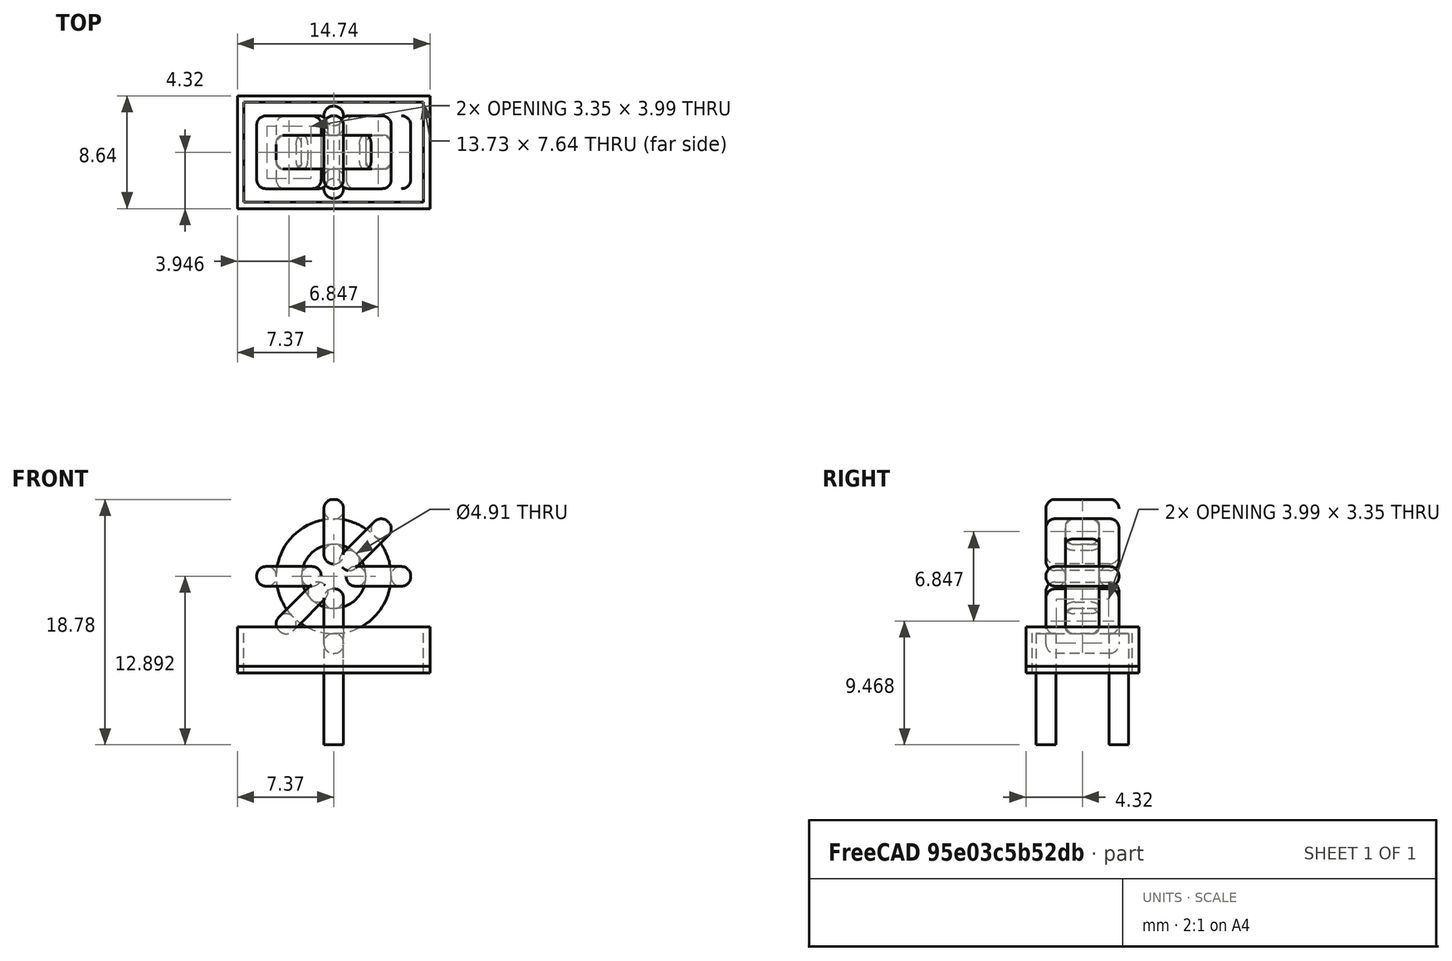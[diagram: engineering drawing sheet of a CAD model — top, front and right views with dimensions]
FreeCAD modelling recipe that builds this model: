
FCSTD DOCUMENT  (FreeCAD 0.16R6703 (Git))
Label: L_Toroid_Vertical_L14.7mm_W8.6mm_P5.58mm_Pulse_KM-1
License: All rights reserved
LicenseURL: http://en.wikipedia.org/wiki/All_rights_reserved
objects: Sketcher::SketchObject×8, PartDesign::Pad×8, PartDesign::Fillet×5, Spreadsheet::Sheet×1
note: 29 computed .brp shape members not serialized (recipe doc carries the construction recipe); baked Part::Feature solids carry a one-line shape summary decoded from their .brp

FEATURE [Spreadsheet::Sheet] Spreadsheet  label="dimensions"
  cells = A1=Wx; B1(Wx)=11.784; C1(WW)=4.91; D1(iWx)=14.73; A2=Wy; B2(Wy)=5.58; D2(iWy)=8.640000000000001; A3=RM; B3(RMx)=5.58; C3(RMy)=0; A4=d_wire; B4(d_wire)=1.5; A5=H; B5(H)=14.73; A6=offsetx; B6(offsetx)=7.365
FEATURE [Sketcher::SketchObject] Sketch
  Placement = pos=(0,-2.79,0) rot=(1,0,0;1.5708rad)
  expr: Placement.Base.y = -Spreadsheet.RMx / 2
  expr: Constraints[0] = Spreadsheet.Wx / 2 - Spreadsheet.d_wire
  expr: Constraints[4] = Spreadsheet.WW / 2
  expr: Constraints[2] = Spreadsheet.Wx / 2 + Spreadsheet.d_wire + 0.5
  sketch-geometry (2):
    g0: Circle CenterX=0 CenterY=7.892 CenterZ=0 NormalX=0 NormalY=0 NormalZ=1 Radius=4.392
    g1: Circle CenterX=0 CenterY=7.892 CenterZ=0 NormalX=0 NormalY=0 NormalZ=1 Radius=2.455
  constraints (5):
    c: Radius(g0) = 4.392
    c: DistanceX(g-1,g0) = 0
    c: DistanceY(g-1,g0) = 7.892
    c: Coincident(g1,g0)
    c: Radius(g1) = 2.455
FEATURE [PartDesign::Pad] Pad
  Length = 2.58
  Length2 = 100
  Midplane = true
  Placement = pos=(0,-2.79,0) rot=(1,0,0;1.5708rad)
  Sketch = -> Sketch
  Type = 0
  expr: Length = Spreadsheet.Wy - 2 * Spreadsheet.d_wire
FEATURE [Sketcher::SketchObject] Sketch001
  Placement = pos=(0,0,2) rot=(0,0,1;0rad)
  expr: Placement.Base.z = 0.5 + Spreadsheet.d_wire
  expr: Constraints[4] = Spreadsheet.RMy
  expr: Constraints[2] = -Spreadsheet.RMx
  expr: Constraints[1] = Spreadsheet.d_wire / 2
  sketch-geometry (2):
    g0: Circle CenterX=0 CenterY=0 CenterZ=0 NormalX=0 NormalY=0 NormalZ=1 Radius=0.75
    g1: Circle CenterX=0 CenterY=-5.58 CenterZ=0 NormalX=0 NormalY=0 NormalZ=1 Radius=0.75
  constraints (5):
    c: Equal(g0,g1)
    c: Radius(g0) = 0.75
    c: DistanceY(g-1,g1) = -5.58
    c: Coincident(g0,g-1)
    c: DistanceX(g-1,g1) = 0
FEATURE [PartDesign::Pad] Pad001
  Length = 1.5
  Length2 = 7
  Placement = pos=(0,0,2) rot=(0,0,1;0rad)
  Reversed = true
  Sketch = -> Sketch001
  Type = 4
  expr: Length2 = 5.5 + Spreadsheet.d_wire
  expr: Length = Spreadsheet.d_wire
FEATURE [PartDesign::Fillet] Fillet
  Base = -> Pad [Edge6,Edge3,Edge2]
  Placement = pos=(0,-2.79,0) rot=(1,0,0;1.5708rad)
  Radius = 0.5
FEATURE [Sketcher::SketchObject] Sketch003
  Placement = pos=(0,0,7.892) rot=(1,0,0;3.14159rad)
  expr: Constraints[18] = Spreadsheet.d_wire
  expr: Constraints[16] = Spreadsheet.d_wire
  expr: Constraints[19] = Spreadsheet.d_wire
  expr: Constraints[17] = Spreadsheet.d_wire
  expr: Placement.Base.y = -1 * (Spreadsheet.RMx - Spreadsheet.Wy) / 2
  expr: Constraints[21] = (Spreadsheet.Wx - Spreadsheet.WW) / 2 - Spreadsheet.d_wire
  expr: Constraints[22] = Spreadsheet.Wx / 2 - Spreadsheet.d_wire
  expr: Constraints[43] = Spreadsheet.d_wire
  expr: Constraints[48] = Spreadsheet.Wx - Spreadsheet.d_wire * 2
  expr: Constraints[49] = Spreadsheet.Wy
  expr: Placement.Base.z = Spreadsheet.Wx / 2 + Spreadsheet.d_wire + 0.5
  sketch-geometry (16):
    g0: LineSegment StartX=-0.955 StartY=0 StartZ=0 EndX=-5.892 EndY=0 EndZ=0
    g1: LineSegment StartX=-5.892 StartY=0 StartZ=0 EndX=-5.892 EndY=5.58 EndZ=0
    g2: LineSegment StartX=-5.892 StartY=5.58 StartZ=0 EndX=-0.955 EndY=5.58 EndZ=0
    g3: LineSegment StartX=-0.955 StartY=5.58 StartZ=0 EndX=-0.955 EndY=0 EndZ=0
    g4: LineSegment StartX=-4.392 StartY=4.08 StartZ=0 EndX=-2.455 EndY=4.08 EndZ=0
    g5: LineSegment StartX=-2.455 StartY=4.08 StartZ=0 EndX=-2.455 EndY=1.5 EndZ=0
    g6: LineSegment StartX=-2.455 StartY=1.5 StartZ=0 EndX=-4.392 EndY=1.5 EndZ=0
    g7: LineSegment StartX=-4.392 StartY=1.5 StartZ=0 EndX=-4.392 EndY=4.08 EndZ=0
    g8: LineSegment StartX=0.955 StartY=5.58 StartZ=0 EndX=5.892 EndY=5.58 EndZ=0
    g9: LineSegment StartX=5.892 StartY=5.58 StartZ=0 EndX=5.892 EndY=0 EndZ=0
    g10: LineSegment StartX=5.892 StartY=0 StartZ=0 EndX=0.955 EndY=0 EndZ=0
    g11: LineSegment StartX=0.955 StartY=0 StartZ=0 EndX=0.955 EndY=5.58 EndZ=0
    g12: LineSegment StartX=2.455 StartY=4.08 StartZ=0 EndX=4.392 EndY=4.08 EndZ=0
    g13: LineSegment StartX=4.392 StartY=4.08 StartZ=0 EndX=4.392 EndY=1.5 EndZ=0
    g14: LineSegment StartX=4.392 StartY=1.5 StartZ=0 EndX=2.455 EndY=1.5 EndZ=0
    g15: LineSegment StartX=2.455 StartY=1.5 StartZ=0 EndX=2.455 EndY=4.08 EndZ=0
  constraints (50):
    c: Horizontal(g0)
    c: Coincident(g1,g0)
    c: Vertical(g1)
    c: Coincident(g2,g1)
    c: Horizontal(g2)
    c: Coincident(g3,g2)
    c: Coincident(g3,g0)
    c: Vertical(g3)
    c: Coincident(g4,g5)
    c: Coincident(g5,g6)
    c: Coincident(g6,g7)
    c: Coincident(g7,g4)
    c: Horizontal(g4)
    c: Horizontal(g6)
    c: Vertical(g5)
    c: Vertical(g7)
    c: DistanceX(g1,g4) = 1.5
    c: DistanceY(g4,g1) = 1.5
    c: DistanceX(g5,g0) = 1.5
    c: DistanceY(g0,g5) = 1.5
    c: DistanceY(g-1,g0) = 0
    c: DistanceX(g6,g6) = 1.937
    c: DistanceX(g6,g-1) = 4.392
    c: Coincident(g8,g9)
    c: Coincident(g9,g10)
    c: Coincident(g10,g11)
    c: Coincident(g11,g8)
    c: Horizontal(g8)
    c: Horizontal(g10)
    c: Vertical(g9)
    c: Vertical(g11)
    c: Coincident(g12,g13)
    c: Coincident(g13,g14)
    c: Coincident(g14,g15)
    c: Coincident(g15,g12)
    c: Horizontal(g12)
    c: Horizontal(g14)
    c: Vertical(g13)
    c: Vertical(g15)
    c: DistanceY(g8,g2) = 0
    c: DistanceY(g10,g0) = 0
    c: DistanceY(g14,g5) = 0
    c: DistanceY(g12,g4) = 0
    c: DistanceX(g8,g12) = 1.5
    c: Equal(g8,g2)
    c: Equal(g12,g4)
    c: Equal(g9,g1)
    c: Equal(g13,g7)
    c: DistanceX(g4,g12) = 8.784
    c: DistanceY(g0,g1) = 5.58
FEATURE [PartDesign::Pad] Pad002
  Length = 1.5
  Length2 = 100
  Midplane = true
  Placement = pos=(0,0,7.892) rot=(1,0,0;3.14159rad)
  Sketch = -> Sketch003
  Type = 0
  expr: Length = Spreadsheet.d_wire
FEATURE [PartDesign::Fillet] Fillet001
  Base = -> Pad002 [Edge38,Edge41,Edge42,Edge43,Edge29,Edge32,Edge33,Edge34,Edge25,Edge35,Edge36,Edge13,Edge14,Edge15,Edge16,Edge17,Edge18,Edge19,Edge1,Edge2,Edge3,Edge4,Edge5,Edge6,Edge7,Edge37,Edge39,Edge40,Edge20,Edge23,Edge24,Edge21,Edge22,Edge8,Edge9,Edge10,Edge11,Edge12,Edge26,Edge27,+8 more]
  Placement = pos=(0,0,7.892) rot=(1,0,0;3.14159rad)
  Radius = 0.705
  expr: Radius = Spreadsheet.d_wire * 0.47
FEATURE [Sketcher::SketchObject] Sketch004
  Placement = pos=(0,0,7.892) rot=(0.92388,0,0.382683;3.14159rad)
  expr: Constraints[18] = Spreadsheet.d_wire
  expr: Constraints[16] = Spreadsheet.d_wire
  expr: Constraints[19] = Spreadsheet.d_wire
  expr: Constraints[17] = Spreadsheet.d_wire
  expr: Placement.Base.y = -1 * (Spreadsheet.RMx - Spreadsheet.Wy) / 2
  expr: Constraints[21] = (Spreadsheet.Wx - Spreadsheet.WW) / 2 - Spreadsheet.d_wire
  expr: Constraints[22] = Spreadsheet.Wx / 2 - Spreadsheet.d_wire
  expr: Constraints[43] = Spreadsheet.d_wire
  expr: Constraints[48] = Spreadsheet.Wx - 2 * Spreadsheet.d_wire
  expr: Constraints[49] = Spreadsheet.Wy
  expr: Placement.Base.z = Spreadsheet.Wx / 2 + Spreadsheet.d_wire + 0.5
  sketch-geometry (16):
    g0: LineSegment StartX=-0.955 StartY=0 StartZ=0 EndX=-5.892 EndY=0 EndZ=0
    g1: LineSegment StartX=-5.892 StartY=0 StartZ=0 EndX=-5.892 EndY=5.58 EndZ=0
    g2: LineSegment StartX=-5.892 StartY=5.58 StartZ=0 EndX=-0.955 EndY=5.58 EndZ=0
    g3: LineSegment StartX=-0.955 StartY=5.58 StartZ=0 EndX=-0.955 EndY=0 EndZ=0
    g4: LineSegment StartX=-4.392 StartY=4.08 StartZ=0 EndX=-2.455 EndY=4.08 EndZ=0
    g5: LineSegment StartX=-2.455 StartY=4.08 StartZ=0 EndX=-2.455 EndY=1.5 EndZ=0
    g6: LineSegment StartX=-2.455 StartY=1.5 StartZ=0 EndX=-4.392 EndY=1.5 EndZ=0
    g7: LineSegment StartX=-4.392 StartY=1.5 StartZ=0 EndX=-4.392 EndY=4.08 EndZ=0
    g8: LineSegment StartX=0.955 StartY=5.58 StartZ=0 EndX=5.892 EndY=5.58 EndZ=0
    g9: LineSegment StartX=5.892 StartY=5.58 StartZ=0 EndX=5.892 EndY=0 EndZ=0
    g10: LineSegment StartX=5.892 StartY=0 StartZ=0 EndX=0.955 EndY=0 EndZ=0
    g11: LineSegment StartX=0.955 StartY=0 StartZ=0 EndX=0.955 EndY=5.58 EndZ=0
    g12: LineSegment StartX=2.455 StartY=4.08 StartZ=0 EndX=4.392 EndY=4.08 EndZ=0
    g13: LineSegment StartX=4.392 StartY=4.08 StartZ=0 EndX=4.392 EndY=1.5 EndZ=0
    g14: LineSegment StartX=4.392 StartY=1.5 StartZ=0 EndX=2.455 EndY=1.5 EndZ=0
    g15: LineSegment StartX=2.455 StartY=1.5 StartZ=0 EndX=2.455 EndY=4.08 EndZ=0
  constraints (50):
    c: Horizontal(g0)
    c: Coincident(g1,g0)
    c: Vertical(g1)
    c: Coincident(g2,g1)
    c: Horizontal(g2)
    c: Coincident(g3,g2)
    c: Coincident(g3,g0)
    c: Vertical(g3)
    c: Coincident(g4,g5)
    c: Coincident(g5,g6)
    c: Coincident(g6,g7)
    c: Coincident(g7,g4)
    c: Horizontal(g4)
    c: Horizontal(g6)
    c: Vertical(g5)
    c: Vertical(g7)
    c: DistanceX(g1,g4) = 1.5
    c: DistanceY(g4,g1) = 1.5
    c: DistanceX(g5,g0) = 1.5
    c: DistanceY(g0,g5) = 1.5
    c: DistanceY(g-1,g0) = 0
    c: DistanceX(g6,g6) = 1.937
    c: DistanceX(g6,g-1) = 4.392
    c: Coincident(g8,g9)
    c: Coincident(g9,g10)
    c: Coincident(g10,g11)
    c: Coincident(g11,g8)
    c: Horizontal(g8)
    c: Horizontal(g10)
    c: Vertical(g9)
    c: Vertical(g11)
    c: Coincident(g12,g13)
    c: Coincident(g13,g14)
    c: Coincident(g14,g15)
    c: Coincident(g15,g12)
    c: Horizontal(g12)
    c: Horizontal(g14)
    c: Vertical(g13)
    c: Vertical(g15)
    c: DistanceY(g8,g2) = 0
    c: DistanceY(g10,g0) = 0
    c: DistanceY(g14,g5) = 0
    c: DistanceY(g12,g4) = 0
    c: DistanceX(g8,g12) = 1.5
    c: Equal(g8,g2)
    c: Equal(g12,g4)
    c: Equal(g9,g1)
    c: Equal(g13,g7)
    c: DistanceX(g4,g12) = 8.784
    c: DistanceY(g0,g1) = 5.58
FEATURE [PartDesign::Pad] Pad003
  Length = 1.5
  Length2 = 100
  Midplane = true
  Placement = pos=(0,0,7.892) rot=(0.92388,0,0.382683;3.14159rad)
  Sketch = -> Sketch004
  Type = 0
  expr: Length = Spreadsheet.d_wire
FEATURE [PartDesign::Fillet] Fillet002
  Base = -> Pad003 [Edge38,Edge41,Edge42,Edge43,Edge29,Edge32,Edge33,Edge34,Edge25,Edge35,Edge36,Edge13,Edge14,Edge15,Edge16,Edge17,Edge18,Edge19,Edge1,Edge2,Edge3,Edge4,Edge5,Edge6,Edge7,Edge37,Edge39,Edge40,Edge20,Edge23,Edge24,Edge21,Edge22,Edge8,Edge9,Edge10,Edge11,Edge12,Edge26,Edge27,+8 more]
  Placement = pos=(0,0,7.892) rot=(0.92388,0,0.382683;3.14159rad)
  Radius = 0.705
  expr: Radius = Spreadsheet.d_wire * 0.47
FEATURE [Sketcher::SketchObject] Sketch005
  Placement = pos=(0,0,7.892) rot=(0.92388,0,-0.382683;3.14159rad)
  expr: Constraints[18] = Spreadsheet.d_wire
  expr: Constraints[16] = Spreadsheet.d_wire
  expr: Constraints[19] = Spreadsheet.d_wire
  expr: Constraints[17] = Spreadsheet.d_wire
  expr: Placement.Base.y = -1 * (Spreadsheet.RMx - Spreadsheet.Wy) / 2
  expr: Constraints[21] = (Spreadsheet.Wx - Spreadsheet.WW) / 2 - Spreadsheet.d_wire
  expr: Constraints[22] = Spreadsheet.Wx / 2 - Spreadsheet.d_wire
  expr: Constraints[43] = Spreadsheet.d_wire
  expr: Constraints[48] = Spreadsheet.Wx - 2 * Spreadsheet.d_wire
  expr: Constraints[49] = Spreadsheet.Wy
  expr: Placement.Base.z = Spreadsheet.Wx / 2 + Spreadsheet.d_wire + 0.5
  sketch-geometry (16):
    g0: LineSegment StartX=-0.955 StartY=0 StartZ=0 EndX=-5.892 EndY=0 EndZ=0
    g1: LineSegment StartX=-5.892 StartY=0 StartZ=0 EndX=-5.892 EndY=5.58 EndZ=0
    g2: LineSegment StartX=-5.892 StartY=5.58 StartZ=0 EndX=-0.955 EndY=5.58 EndZ=0
    g3: LineSegment StartX=-0.955 StartY=5.58 StartZ=0 EndX=-0.955 EndY=0 EndZ=0
    g4: LineSegment StartX=-4.392 StartY=4.08 StartZ=0 EndX=-2.455 EndY=4.08 EndZ=0
    g5: LineSegment StartX=-2.455 StartY=4.08 StartZ=0 EndX=-2.455 EndY=1.5 EndZ=0
    g6: LineSegment StartX=-2.455 StartY=1.5 StartZ=0 EndX=-4.392 EndY=1.5 EndZ=0
    g7: LineSegment StartX=-4.392 StartY=1.5 StartZ=0 EndX=-4.392 EndY=4.08 EndZ=0
    g8: LineSegment StartX=0.955 StartY=5.58 StartZ=0 EndX=5.892 EndY=5.58 EndZ=0
    g9: LineSegment StartX=5.892 StartY=5.58 StartZ=0 EndX=5.892 EndY=0 EndZ=0
    g10: LineSegment StartX=5.892 StartY=0 StartZ=0 EndX=0.955 EndY=0 EndZ=0
    g11: LineSegment StartX=0.955 StartY=0 StartZ=0 EndX=0.955 EndY=5.58 EndZ=0
    g12: LineSegment StartX=2.455 StartY=4.08 StartZ=0 EndX=4.392 EndY=4.08 EndZ=0
    g13: LineSegment StartX=4.392 StartY=4.08 StartZ=0 EndX=4.392 EndY=1.5 EndZ=0
    g14: LineSegment StartX=4.392 StartY=1.5 StartZ=0 EndX=2.455 EndY=1.5 EndZ=0
    g15: LineSegment StartX=2.455 StartY=1.5 StartZ=0 EndX=2.455 EndY=4.08 EndZ=0
  constraints (50):
    c: Horizontal(g0)
    c: Coincident(g1,g0)
    c: Vertical(g1)
    c: Coincident(g2,g1)
    c: Horizontal(g2)
    c: Coincident(g3,g2)
    c: Coincident(g3,g0)
    c: Vertical(g3)
    c: Coincident(g4,g5)
    c: Coincident(g5,g6)
    c: Coincident(g6,g7)
    c: Coincident(g7,g4)
    c: Horizontal(g4)
    c: Horizontal(g6)
    c: Vertical(g5)
    c: Vertical(g7)
    c: DistanceX(g1,g4) = 1.5
    c: DistanceY(g4,g1) = 1.5
    c: DistanceX(g5,g0) = 1.5
    c: DistanceY(g0,g5) = 1.5
    c: DistanceY(g-1,g0) = 0
    c: DistanceX(g6,g6) = 1.937
    c: DistanceX(g6,g-1) = 4.392
    c: Coincident(g8,g9)
    c: Coincident(g9,g10)
    c: Coincident(g10,g11)
    c: Coincident(g11,g8)
    c: Horizontal(g8)
    c: Horizontal(g10)
    c: Vertical(g9)
    c: Vertical(g11)
    c: Coincident(g12,g13)
    c: Coincident(g13,g14)
    c: Coincident(g14,g15)
    c: Coincident(g15,g12)
    c: Horizontal(g12)
    c: Horizontal(g14)
    c: Vertical(g13)
    c: Vertical(g15)
    c: DistanceY(g8,g2) = 0
    c: DistanceY(g10,g0) = 0
    c: DistanceY(g14,g5) = 0
    c: DistanceY(g12,g4) = 0
    c: DistanceX(g8,g12) = 1.5
    c: Equal(g8,g2)
    c: Equal(g12,g4)
    c: Equal(g9,g1)
    c: Equal(g13,g7)
    c: DistanceX(g4,g12) = 8.784
    c: DistanceY(g0,g1) = 5.58
FEATURE [PartDesign::Pad] Pad004
  Length = 1.5
  Length2 = 100
  Midplane = true
  Placement = pos=(0,0,7.892) rot=(0.92388,0,-0.382683;3.14159rad)
  Sketch = -> Sketch005
  Type = 0
  expr: Length = Spreadsheet.d_wire
FEATURE [PartDesign::Fillet] Fillet003
  Base = -> Pad004 [Edge38,Edge41,Edge42,Edge43,Edge29,Edge32,Edge33,Edge34,Edge25,Edge35,Edge36,Edge13,Edge14,Edge15,Edge16,Edge17,Edge18,Edge19,Edge1,Edge2,Edge3,Edge4,Edge5,Edge6,Edge7,Edge37,Edge39,Edge40,Edge20,Edge23,Edge24,Edge21,Edge22,Edge8,Edge9,Edge10,Edge11,Edge12,Edge26,Edge27,+8 more]
  Placement = pos=(0,0,7.892) rot=(0.92388,0,-0.382683;3.14159rad)
  Radius = 0.705
  expr: Radius = Spreadsheet.d_wire * 0.47
FEATURE [Sketcher::SketchObject] Sketch006
  Placement = pos=(0,0,7.892) rot=(0.707107,0,0.707107;3.14159rad)
  expr: Constraints[18] = Spreadsheet.d_wire
  expr: Constraints[16] = Spreadsheet.d_wire
  expr: Constraints[19] = Spreadsheet.d_wire
  expr: Constraints[17] = Spreadsheet.d_wire
  expr: Placement.Base.y = -1 * (Spreadsheet.RMx - Spreadsheet.Wy) / 2
  expr: Constraints[21] = (Spreadsheet.Wx - Spreadsheet.WW) / 2 - Spreadsheet.d_wire
  expr: Constraints[22] = Spreadsheet.Wx / 2 - Spreadsheet.d_wire
  expr: Constraints[43] = Spreadsheet.d_wire
  expr: Constraints[48] = Spreadsheet.Wx - Spreadsheet.d_wire * 2
  expr: Constraints[49] = Spreadsheet.Wy
  expr: Placement.Base.z = Spreadsheet.Wx / 2 + Spreadsheet.d_wire + 0.5
  sketch-geometry (16):
    g0: LineSegment StartX=-0.955 StartY=0 StartZ=0 EndX=-5.892 EndY=0 EndZ=0
    g1: LineSegment StartX=-5.892 StartY=0 StartZ=0 EndX=-5.892 EndY=5.58 EndZ=0
    g2: LineSegment StartX=-5.892 StartY=5.58 StartZ=0 EndX=-0.955 EndY=5.58 EndZ=0
    g3: LineSegment StartX=-0.955 StartY=5.58 StartZ=0 EndX=-0.955 EndY=0 EndZ=0
    g4: LineSegment StartX=-4.392 StartY=4.08 StartZ=0 EndX=-2.455 EndY=4.08 EndZ=0
    g5: LineSegment StartX=-2.455 StartY=4.08 StartZ=0 EndX=-2.455 EndY=1.5 EndZ=0
    g6: LineSegment StartX=-2.455 StartY=1.5 StartZ=0 EndX=-4.392 EndY=1.5 EndZ=0
    g7: LineSegment StartX=-4.392 StartY=1.5 StartZ=0 EndX=-4.392 EndY=4.08 EndZ=0
    g8: LineSegment StartX=0.955 StartY=5.58 StartZ=0 EndX=5.892 EndY=5.58 EndZ=0
    g9: LineSegment StartX=5.892 StartY=5.58 StartZ=0 EndX=5.892 EndY=0 EndZ=0
    g10: LineSegment StartX=5.892 StartY=0 StartZ=0 EndX=0.955 EndY=0 EndZ=0
    g11: LineSegment StartX=0.955 StartY=0 StartZ=0 EndX=0.955 EndY=5.58 EndZ=0
    g12: LineSegment StartX=2.455 StartY=4.08 StartZ=0 EndX=4.392 EndY=4.08 EndZ=0
    g13: LineSegment StartX=4.392 StartY=4.08 StartZ=0 EndX=4.392 EndY=1.5 EndZ=0
    g14: LineSegment StartX=4.392 StartY=1.5 StartZ=0 EndX=2.455 EndY=1.5 EndZ=0
    g15: LineSegment StartX=2.455 StartY=1.5 StartZ=0 EndX=2.455 EndY=4.08 EndZ=0
  constraints (50):
    c: Horizontal(g0)
    c: Coincident(g1,g0)
    c: Vertical(g1)
    c: Coincident(g2,g1)
    c: Horizontal(g2)
    c: Coincident(g3,g2)
    c: Coincident(g3,g0)
    c: Vertical(g3)
    c: Coincident(g4,g5)
    c: Coincident(g5,g6)
    c: Coincident(g6,g7)
    c: Coincident(g7,g4)
    c: Horizontal(g4)
    c: Horizontal(g6)
    c: Vertical(g5)
    c: Vertical(g7)
    c: DistanceX(g1,g4) = 1.5
    c: DistanceY(g4,g1) = 1.5
    c: DistanceX(g5,g0) = 1.5
    c: DistanceY(g0,g5) = 1.5
    c: DistanceY(g-1,g0) = 0
    c: DistanceX(g6,g6) = 1.937
    c: DistanceX(g6,g-1) = 4.392
    c: Coincident(g8,g9)
    c: Coincident(g9,g10)
    c: Coincident(g10,g11)
    c: Coincident(g11,g8)
    c: Horizontal(g8)
    c: Horizontal(g10)
    c: Vertical(g9)
    c: Vertical(g11)
    c: Coincident(g12,g13)
    c: Coincident(g13,g14)
    c: Coincident(g14,g15)
    c: Coincident(g15,g12)
    c: Horizontal(g12)
    c: Horizontal(g14)
    c: Vertical(g13)
    c: Vertical(g15)
    c: DistanceY(g8,g2) = 0
    c: DistanceY(g10,g0) = 0
    c: DistanceY(g14,g5) = 0
    c: DistanceY(g12,g4) = 0
    c: DistanceX(g8,g12) = 1.5
    c: Equal(g8,g2)
    c: Equal(g12,g4)
    c: Equal(g9,g1)
    c: Equal(g13,g7)
    c: DistanceX(g4,g12) = 8.784
    c: DistanceY(g0,g1) = 5.58
FEATURE [PartDesign::Pad] Pad005
  Length = 1.5
  Length2 = 100
  Midplane = true
  Placement = pos=(0,0,7.892) rot=(0.707107,0,0.707107;3.14159rad)
  Sketch = -> Sketch006
  Type = 0
  expr: Length = Spreadsheet.d_wire
FEATURE [PartDesign::Fillet] Fillet004
  Base = -> Pad005 [Edge38,Edge41,Edge42,Edge43,Edge29,Edge32,Edge33,Edge34,Edge25,Edge35,Edge36,Edge13,Edge14,Edge15,Edge16,Edge17,Edge18,Edge19,Edge1,Edge2,Edge3,Edge4,Edge5,Edge6,Edge7,Edge37,Edge39,Edge40,Edge20,Edge23,Edge24,Edge21,Edge22,Edge8,Edge9,Edge10,Edge11,Edge12,Edge26,Edge27,+8 more]
  Placement = pos=(0,0,7.892) rot=(0.707107,0,0.707107;3.14159rad)
  Radius = 0.705
  expr: Radius = Spreadsheet.d_wire * 0.47
FEATURE [Sketcher::SketchObject] Sketch007
  Placement = pos=(0,0,0.5) rot=(0,0,1;0rad)
  expr: Placement.Base.z = 0.5
  expr: Constraints[11] = Spreadsheet.iWx / 2
  expr: Constraints[10] = (Spreadsheet.iWy - Spreadsheet.RMx) / 2
  expr: Constraints[9] = Spreadsheet.iWy
  expr: Constraints[8] = Spreadsheet.iWx
  sketch-geometry (4):
    g0: LineSegment StartX=-7.365 StartY=1.53 StartZ=0 EndX=7.365 EndY=1.53 EndZ=0
    g1: LineSegment StartX=7.365 StartY=1.53 StartZ=0 EndX=7.365 EndY=-7.11 EndZ=0
    g2: LineSegment StartX=7.365 StartY=-7.11 StartZ=0 EndX=-7.365 EndY=-7.11 EndZ=0
    g3: LineSegment StartX=-7.365 StartY=-7.11 StartZ=0 EndX=-7.365 EndY=1.53 EndZ=0
  constraints (12):
    c: Coincident(g0,g1)
    c: Coincident(g1,g2)
    c: Coincident(g2,g3)
    c: Coincident(g3,g0)
    c: Horizontal(g0)
    c: Horizontal(g2)
    c: Vertical(g1)
    c: Vertical(g3)
    c: DistanceX(g0,g0) = 14.73
    c: DistanceY(g3,g3) = 8.64
    c: DistanceY(g-1,g0) = 1.53
    c: DistanceX(g0,g-1) = 7.365
FEATURE [PartDesign::Pad] Pad006
  Length = 0.5
  Length2 = 100
  Placement = pos=(0,0,0.5) rot=(0,0,1;0rad)
  Sketch = -> Sketch007
  Type = 0
FEATURE [Sketcher::SketchObject] Sketch008
  Placement = pos=(0,0,0.5) rot=(0,0,1;0rad)
  expr: Constraints[8] = Spreadsheet.iWx
  expr: Constraints[9] = Spreadsheet.iWy
  expr: Constraints[10] = (Spreadsheet.iWy - Spreadsheet.RMx) / 2
  expr: Placement.Base.z = 0.5
  expr: Constraints[21] = 0.5
  expr: Constraints[11] = Spreadsheet.iWx / 2
  sketch-geometry (8):
    g0: LineSegment StartX=-7.365 StartY=1.53 StartZ=0 EndX=7.365 EndY=1.53 EndZ=0
    g1: LineSegment StartX=7.365 StartY=1.53 StartZ=0 EndX=7.365 EndY=-7.11 EndZ=0
    g2: LineSegment StartX=7.365 StartY=-7.11 StartZ=0 EndX=-7.365 EndY=-7.11 EndZ=0
    g3: LineSegment StartX=-7.365 StartY=-7.11 StartZ=0 EndX=-7.365 EndY=1.53 EndZ=0
    g4: LineSegment StartX=-6.865 StartY=1.03 StartZ=0 EndX=6.865 EndY=1.03 EndZ=0
    g5: LineSegment StartX=6.865 StartY=1.03 StartZ=0 EndX=6.865 EndY=-6.61 EndZ=0
    g6: LineSegment StartX=6.865 StartY=-6.61 StartZ=0 EndX=-6.865 EndY=-6.61 EndZ=0
    g7: LineSegment StartX=-6.865 StartY=-6.61 StartZ=0 EndX=-6.865 EndY=1.03 EndZ=0
  constraints (24):
    c: Coincident(g0,g1)
    c: Coincident(g1,g2)
    c: Coincident(g2,g3)
    c: Coincident(g3,g0)
    c: Horizontal(g0)
    c: Horizontal(g2)
    c: Vertical(g1)
    c: Vertical(g3)
    c: DistanceX(g0,g0) = 14.73
    c: DistanceY(g3,g3) = 8.64
    c: DistanceY(g-1,g0) = 1.53
    c: DistanceX(g0,g-1) = 7.365
    c: Coincident(g4,g5)
    c: Coincident(g5,g6)
    c: Coincident(g6,g7)
    c: Coincident(g7,g4)
    c: Horizontal(g4)
    c: Horizontal(g6)
    c: Vertical(g5)
    c: Vertical(g7)
    c: DistanceX(g5,g1) = 0.5
    c: DistanceY(g1,g5) = 0.5
    c: DistanceX(g0,g4) = 0.5
    c: DistanceY(g4,g0) = 0.5
FEATURE [PartDesign::Pad] Pad007
  Length = 3.5352
  Length2 = 100
  Placement = pos=(0,0,0.5) rot=(0,0,1;0rad)
  Sketch = -> Sketch008
  Type = 0
  expr: Length = Spreadsheet.Wx * 0.3
